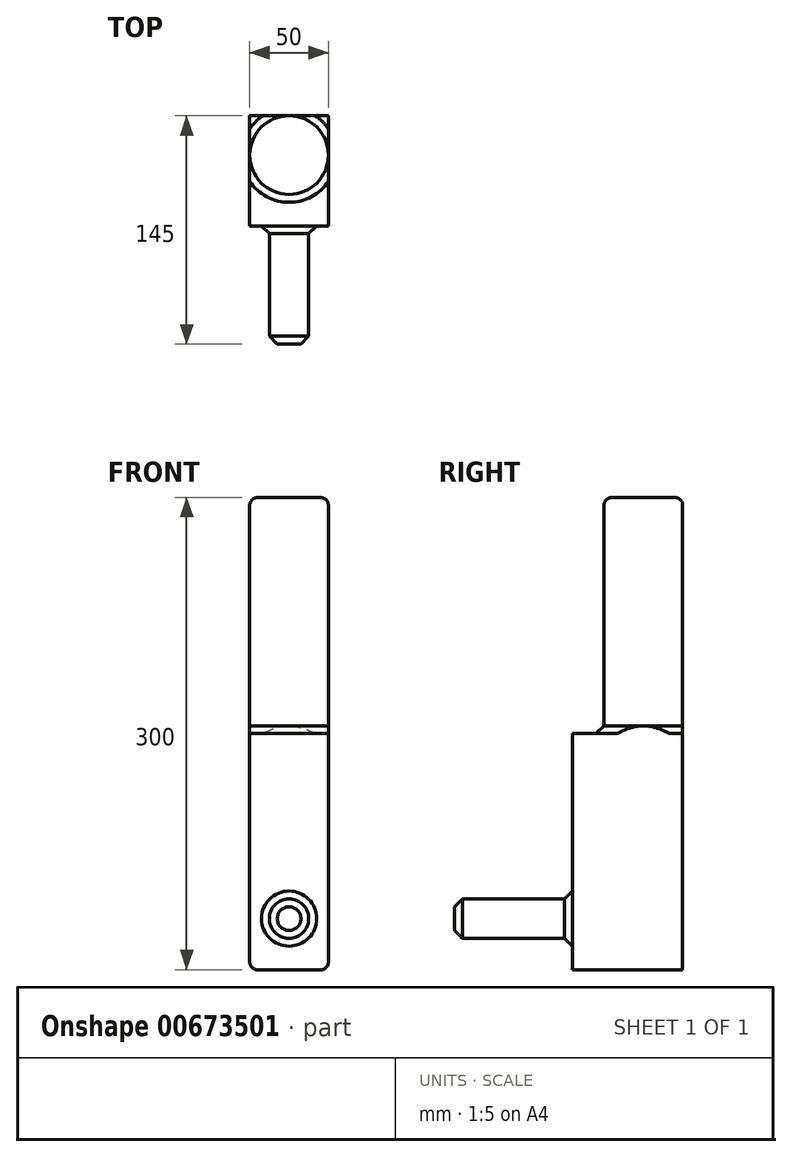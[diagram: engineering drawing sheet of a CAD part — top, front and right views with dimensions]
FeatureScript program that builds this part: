
annotation { "Feature Type Name" : "Feature", "Feature Type Description" : "" }
export const myFeature = defineFeature(function(context is Context, id is Id, definition is map)
    precondition{}
    {
        {
            var Q0;
            Q0=qCreatedBy(makeId("Top.planeOp"),FACE);
            var sketch = newSketch(context, id + "F0", { "sketchPlane" : qUnion([Q0])});
            skCircle(sketch, "E0", {"center": v(0, 0) * mm, "radius": 25 * mm});
            skSolve(sketch);
        }
        {
            var Q0;
            Q0=qCreatedBy(makeId("Right.planeOp"),FACE);
            var sketch = newSketch(context, id + "F1", { "sketchPlane" : qUnion([Q0])});
            skLineSegment(sketch, "E1.bottom", {"start": v(-45, 0) * mm, "end": v(25, 0) * mm});
            skLineSegment(sketch, "E1.top", {"start": v(-45, -150) * mm, "end": v(25, -150) * mm});
            skLineSegment(sketch, "E1.left", {"start": v(-45, 0) * mm, "end": v(-45, -150) * mm});
            skLineSegment(sketch, "E1.right", {"start": v(25, 0) * mm, "end": v(25, -150) * mm});
            skSolve(sketch);
        }
        {
            var Q0;
            Q0=makeQuery(id+"F1.imprint","IMPRINT",FACE,{"disambiguationData":[TD([[makeQuery(id+"F1.imprint","IMPRINT",EDGE,{"derivedFrom":sQuery(id+"F1.wireOp",EDGE,"E1.bottom")}),-1.0]])]});
            extrude(context, id + "F2", {"entities" : qUnion([Q0]), "endBound" : BoundingType.SYMMETRIC, "depth" : 50 * mm, "offsetDistance" : 25 * mm});
        }
        {
            var Q0;
            Q0=qSketchRegion(id+"F0",true);
            extrude(context, id + "F3", {"entities" : qUnion([Q0]), "operationType" : NewBodyOperationType.ADD, "depth" : 150 * mm, "offsetDistance" : 25 * mm});
        }
        {
            var Q0;
            Q0=makeQuery(id+"F3.opExtrude","CAP_EDGE",EDGE,{"disambiguationData":[OSD([sQuery(id+"F0.wireOp",EDGE,"E0")])],"isStart":false});
            fillet(context, id + "F4", {"entities" : qUnion([Q0]), "radius" : 5 * mm, "tangentPropagation" : true, "allowEdgeOverflow" : false});
        }
        {
            var Q0;
            Q0=makeQuery(id+"F2.opExtrude","CAP_EDGE",EDGE,{"disambiguationData":[OSD([sQuery(id+"F1.wireOp",EDGE,"E1.top")])],"isStart":true});
            fillet(context, id + "F5", {"entities" : qUnion([Q0]), "radius" : 5 * mm, "tangentPropagation" : true, "allowEdgeOverflow" : false});
        }
        {
            var Q0;
            Q0=makeQuery(id+"F2.opExtrude","CAP_EDGE",EDGE,{"disambiguationData":[OSD([sQuery(id+"F1.wireOp",EDGE,"E1.top")])],"isStart":false});
            fillet(context, id + "F6", {"entities" : qUnion([Q0]), "radius" : 5 * mm, "tangentPropagation" : true, "allowEdgeOverflow" : false});
        }
        {
            var Q0;
            {var subQ0=sQuery(id+"F1.wireOp",EDGE,"E1.bottom");var subQ1=sQuery(id+"F1.wireOp",EDGE,"E1.left");var subQ2=sQuery(id+"F0.wireOp",EDGE,"E0");Q0=makeQuery(id+"F3.boolean.opBoolean","SPLIT",EDGE,{"disambiguationData":[TD([makeQuery(id+"F2.opExtrude","SWEPT_FACE",FACE,{"disambiguationData":[OSD([subQ0])]}),makeQuery(id+"F2.opExtrude","CAP_FACE",FACE,{"disambiguationData":[OSD([subQ0,sQuery(id+"F1.wireOp",EDGE,"E1.top"),subQ1,sQuery(id+"F1.wireOp",EDGE,"E1.right")])],"isStart":true}),makeQuery(id+"F2.opExtrude","SWEPT_FACE",FACE,{"disambiguationData":[OSD([subQ1])]}),makeQuery(id+"F3.opExtrude","SWEPT_FACE",FACE,{"disambiguationData":[OSD([subQ2])]})])],"derivedFrom":makeQuery(id+"F3.opExtrude","CAP_EDGE",EDGE,{"disambiguationData":[OSD([subQ2])],"isStart":true})});}
            chamfer(context, id + "F7", {"entities" : qUnion([Q0]), "width" : 5 * mm, "tangentPropagation" : true});
        }
        {
            var Q0;
            Q0=qCreatedBy(makeId("Front.planeOp"),FACE);
            var sketch = newSketch(context, id + "F8", { "sketchPlane" : qUnion([Q0])});
            skCircle(sketch, "E2", {"center": v(0, -117.5) * mm, "radius": 12.5 * mm});
            skSolve(sketch);
        }
        {
            var Q0;
            Q0=qSketchRegion(id+"F8",true);
            extrude(context, id + "F9", {"entities" : qUnion([Q0]), "operationType" : NewBodyOperationType.ADD, "depth" : 120 * mm, "offsetDistance" : 25 * mm});
        }
        {
            var Q0;
            Q0=makeQuery(id+"F9.opExtrude","CAP_FACE",FACE,{"disambiguationData":[OSD([sQuery(id+"F8.wireOp",EDGE,"E2")])],"isStart":false});
            var Q1;
            Q1=makeQuery(id+"F9.boolean.opBoolean","INTERSECT",EDGE,{"derivedFrom":[makeQuery(id+"F2.opExtrude","SWEPT_FACE",FACE,{"disambiguationData":[OSD([sQuery(id+"F1.wireOp",EDGE,"E1.left")])]}),makeQuery(id+"F9.opExtrude","SWEPT_FACE",FACE,{"disambiguationData":[OSD([sQuery(id+"F8.wireOp",EDGE,"E2")])]})]});
            chamfer(context, id + "F10", {"entities" : qUnion([Q0, Q1]), "width" : 5 * mm, "tangentPropagation" : true});
        }
    });
